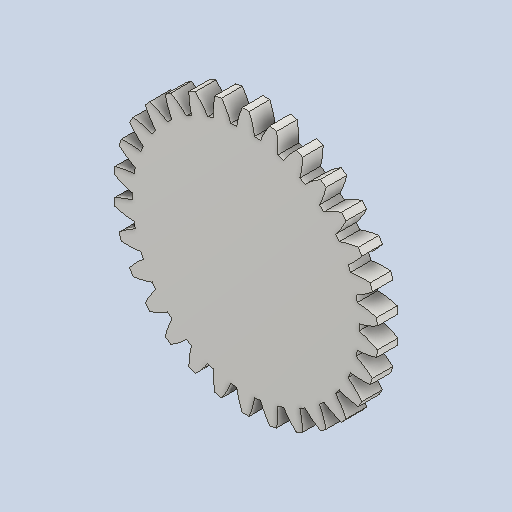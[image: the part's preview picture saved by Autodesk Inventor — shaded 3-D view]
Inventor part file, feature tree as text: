
AUTODESK INVENTOR PART (.ipt)
format: ipt  version: 2024 (Build 280153000, 153)  size: 259,584 bytes
history: native  units: mm (DEFAULTED — no unit token found)
features: plane x3, other x3, extrude x1, sketch x1
ambient origin geometry x8: Origin, YZ Plane, XZ Plane, XY Plane, X Axis, Y Axis, Z Axis, Center Point
bodies: Solid1 (feature_tree)
feature tree (8):
  extrude  "Extrusion1"  Depth=5.0mm TaperAngle=0.0deg
  plane  "Work Plane2"
  plane  "Work Plane8"
  plane  "Work Plane9"
  other  "Spur Gear"
  sketch  "Sketch1"  dims[d0=64.0mm d1=5.0mm d2=0.0mm d3=60.0mm d4=10.0mm d5=0.0mm d16=40.0mm d17=0.0mm d34=1.047198mm d39=0.0mm d41=0.0mm d43=40.0mm d46=40.0mm d47=0.0mm d48=0.0mm]
  other  "Srf1"
  other  "Pitch Diameter"
